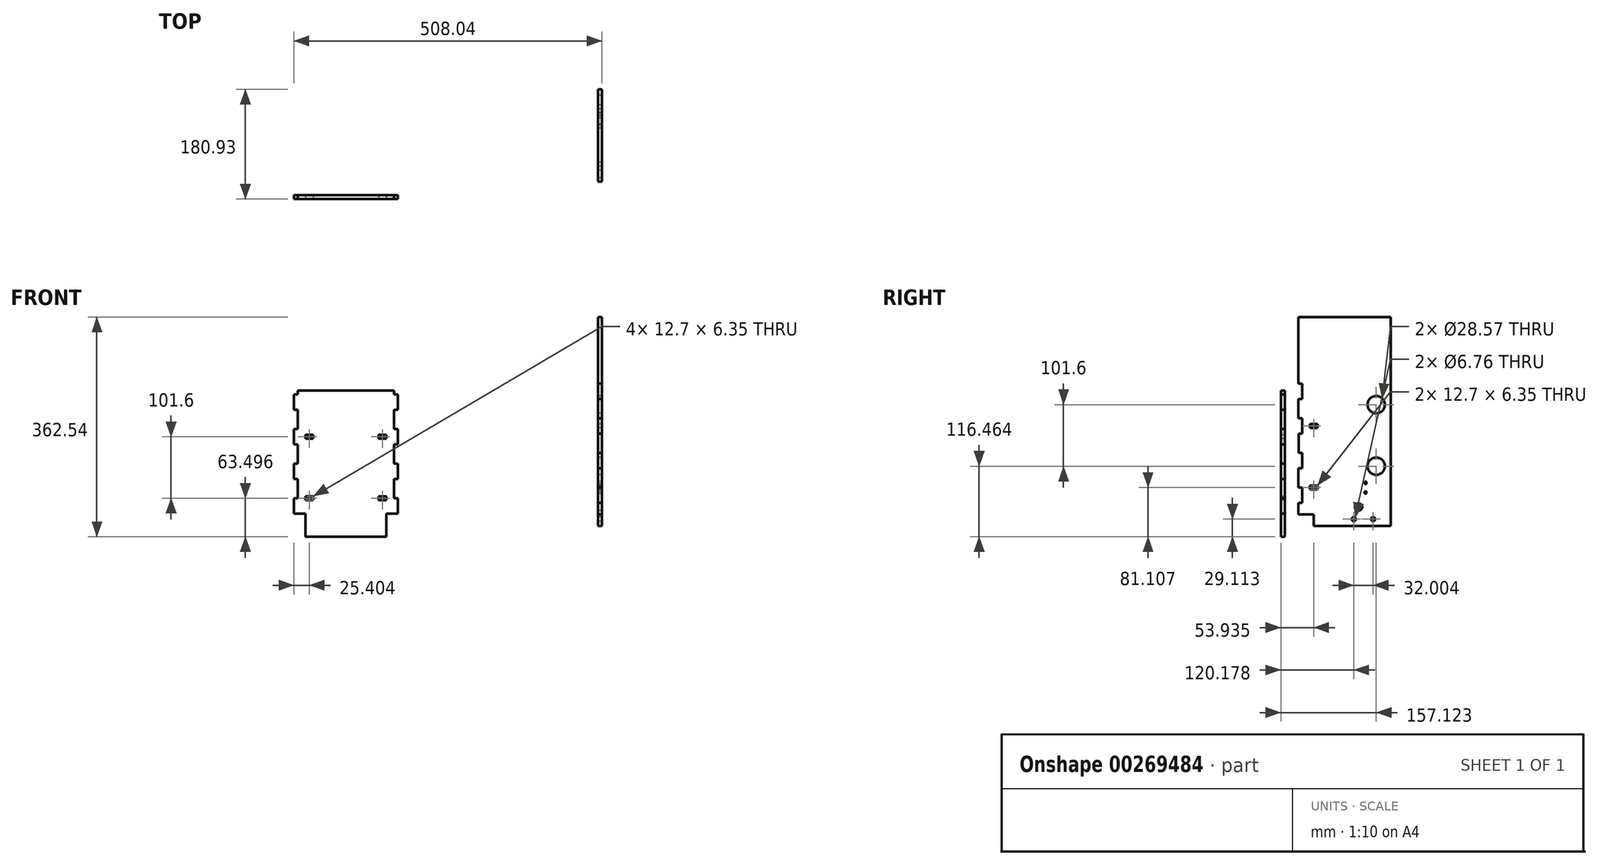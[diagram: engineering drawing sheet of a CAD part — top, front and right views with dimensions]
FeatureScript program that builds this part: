
annotation { "Feature Type Name" : "Feature", "Feature Type Description" : "" }
export const myFeature = defineFeature(function(context is Context, id is Id, definition is map)
    precondition{}
    {
        {
            var Q0;
            Q0=qCreatedBy(makeId("Front.planeOp"),FACE);
            var sketch = newSketch(context, id + "F0", { "sketchPlane" : qUnion([Q0])});
            skLineSegment(sketch, "E0.top", {"start": v(-501.69, -243.4) * mm, "end": v(-330.24, -243.4) * mm});
            skLineSegment(sketch, "E1", {"start": v(-495.34, -2.1) * mm, "end": v(-495.34, -243.4) * mm});
            skLineSegment(sketch, "E2", {"start": v(-501.69, -8.44) * mm, "end": v(-495.34, -8.44) * mm});
            skLineSegment(sketch, "E3", {"start": v(-501.69, -33.84) * mm, "end": v(-495.34, -33.84) * mm});
            skLineSegment(sketch, "E4", {"start": v(-501.69, -65.6) * mm, "end": v(-495.34, -65.6) * mm});
            skLineSegment(sketch, "E5", {"start": v(-501.69, -91) * mm, "end": v(-495.34, -91) * mm});
            skLineSegment(sketch, "E6", {"start": v(-501.69, -122.74) * mm, "end": v(-495.34, -122.74) * mm});
            skLineSegment(sketch, "E7", {"start": v(-501.69, -148.14) * mm, "end": v(-495.34, -148.14) * mm});
            skLineSegment(sketch, "E8", {"start": v(-501.69, -179.9) * mm, "end": v(-495.34, -179.9) * mm});
            skLineSegment(sketch, "E9", {"start": v(-501.69, -205.3) * mm, "end": v(-495.34, -205.3) * mm});
            skLineSegment(sketch, "E10", {"start": v(-501.69, -237.04) * mm, "end": v(-495.34, -237.04) * mm});
            skLineSegment(sketch, "E11", {"start": v(-501.69, -8.44) * mm, "end": v(-501.69, -33.84) * mm});
            skLineSegment(sketch, "E12", {"start": v(-501.69, -65.6) * mm, "end": v(-501.69, -91) * mm});
            skLineSegment(sketch, "E13", {"start": v(-501.69, -122.74) * mm, "end": v(-501.69, -148.14) * mm});
            skLineSegment(sketch, "E14", {"start": v(-501.69, -179.9) * mm, "end": v(-501.69, -205.3) * mm});
            skLineSegment(sketch, "E15", {"start": v(-501.69, -237.04) * mm, "end": v(-501.69, -243.4) * mm});
            skLineSegment(sketch, "E16", {"start": v(-336.59, -2.1) * mm, "end": v(-336.59, -243.4) * mm});
            skLineSegment(sketch, "E17", {"start": v(-336.59, -8.44) * mm, "end": v(-330.24, -8.44) * mm});
            skLineSegment(sketch, "E18", {"start": v(-336.59, -33.84) * mm, "end": v(-330.24, -33.84) * mm});
            skLineSegment(sketch, "E19", {"start": v(-336.59, -65.6) * mm, "end": v(-330.24, -65.6) * mm});
            skLineSegment(sketch, "E20", {"start": v(-336.59, -91) * mm, "end": v(-330.24, -91) * mm});
            skLineSegment(sketch, "E21", {"start": v(-336.59, -122.74) * mm, "end": v(-330.24, -122.74) * mm});
            skLineSegment(sketch, "E22", {"start": v(-336.59, -148.14) * mm, "end": v(-330.24, -148.14) * mm});
            skLineSegment(sketch, "E23", {"start": v(-336.59, -179.9) * mm, "end": v(-330.24, -179.9) * mm});
            skLineSegment(sketch, "E24", {"start": v(-336.59, -205.3) * mm, "end": v(-330.24, -205.3) * mm});
            skLineSegment(sketch, "E25", {"start": v(-336.59, -237.04) * mm, "end": v(-330.24, -237.04) * mm});
            skLineSegment(sketch, "E26", {"start": v(-330.24, -8.44) * mm, "end": v(-330.24, -33.84) * mm});
            skLineSegment(sketch, "E27", {"start": v(-330.24, -65.6) * mm, "end": v(-330.24, -91) * mm});
            skLineSegment(sketch, "E28", {"start": v(-330.24, -122.74) * mm, "end": v(-330.24, -148.14) * mm});
            skLineSegment(sketch, "E29", {"start": v(-330.24, -179.9) * mm, "end": v(-330.24, -205.3) * mm});
            skLineSegment(sketch, "E30", {"start": v(-330.24, -237.04) * mm, "end": v(-330.24, -243.4) * mm});
            skLineSegment(sketch, "E31", {"start": v(-495.34, -2.1) * mm, "end": v(-336.59, -2.1) * mm});
            skSolve(sketch);
        }
        {
            var Q0;
            {var subQ5=sQuery(id+"F0.wireOp",EDGE,"E0.bottom");var subQ8=sQuery(id+"F0.wireOp",EDGE,"E1");var subQ20=makeQuery(id+"F0.imprint","INTERSECT",VERTEX,{"derivedFrom":[subQ5,subQ8]});Q0=makeQuery(id+"F0.imprint","IMPRINT",FACE,{"disambiguationData":[TD([[makeQuery(id+"F0.imprint","IMPRINT",EDGE,{"disambiguationData":[TD([[subQ20,-1.0]])],"derivedFrom":subQ5}),-1.0]])]});}
            var Q1;
            {var subQ4=sQuery(id+"F0.wireOp",EDGE,"LMsAul2w-vVBP-qz1e-n2hl-ZY3DGVZ1hmQM");Q1=makeQuery(id+"F0.imprint","IMPRINT",FACE,{"disambiguationData":[TD([[makeQuery(id+"F0.imprint","IMPRINT",EDGE,{"derivedFrom":subQ4}),1.0]])]});}
            var Q2;
            {var subQ0=sQuery(id+"F0.wireOp",EDGE,"E2");Q2=makeQuery(id+"F0.imprint","IMPRINT",FACE,{"disambiguationData":[TD([[makeQuery(id+"F0.imprint","IMPRINT",EDGE,{"derivedFrom":subQ0}),-1.0]])]});}
            var Q3;
            {var subQ0=sQuery(id+"F0.wireOp",EDGE,"E4");Q3=makeQuery(id+"F0.imprint","IMPRINT",FACE,{"disambiguationData":[TD([[makeQuery(id+"F0.imprint","IMPRINT",EDGE,{"derivedFrom":subQ0}),-1.0]])]});}
            var Q4;
            {var subQ0=sQuery(id+"F0.wireOp",EDGE,"E6");Q4=makeQuery(id+"F0.imprint","IMPRINT",FACE,{"disambiguationData":[TD([[makeQuery(id+"F0.imprint","IMPRINT",EDGE,{"derivedFrom":subQ0}),-1.0]])]});}
            var Q5;
            {var subQ0=sQuery(id+"F0.wireOp",EDGE,"E8");Q5=makeQuery(id+"F0.imprint","IMPRINT",FACE,{"disambiguationData":[TD([[makeQuery(id+"F0.imprint","IMPRINT",EDGE,{"derivedFrom":subQ0}),-1.0]])]});}
            var Q6;
            {var subQ4=sQuery(id+"F0.wireOp",EDGE,"E10");Q6=makeQuery(id+"F0.imprint","IMPRINT",FACE,{"disambiguationData":[TD([[makeQuery(id+"F0.imprint","IMPRINT",EDGE,{"derivedFrom":subQ4}),-1.0]])]});}
            var Q7;
            {var subQ4=sQuery(id+"F0.wireOp",EDGE,"E25");Q7=makeQuery(id+"F0.imprint","IMPRINT",FACE,{"disambiguationData":[TD([[makeQuery(id+"F0.imprint","IMPRINT",EDGE,{"derivedFrom":subQ4}),-1.0]])]});}
            var Q8;
            {var subQ0=sQuery(id+"F0.wireOp",EDGE,"E23");Q8=makeQuery(id+"F0.imprint","IMPRINT",FACE,{"disambiguationData":[TD([[makeQuery(id+"F0.imprint","IMPRINT",EDGE,{"derivedFrom":subQ0}),-1.0]])]});}
            var Q9;
            {var subQ0=sQuery(id+"F0.wireOp",EDGE,"E21");Q9=makeQuery(id+"F0.imprint","IMPRINT",FACE,{"disambiguationData":[TD([[makeQuery(id+"F0.imprint","IMPRINT",EDGE,{"derivedFrom":subQ0}),-1.0]])]});}
            var Q10;
            {var subQ0=sQuery(id+"F0.wireOp",EDGE,"E19");Q10=makeQuery(id+"F0.imprint","IMPRINT",FACE,{"disambiguationData":[TD([[makeQuery(id+"F0.imprint","IMPRINT",EDGE,{"derivedFrom":subQ0}),-1.0]])]});}
            var Q11;
            {var subQ0=sQuery(id+"F0.wireOp",EDGE,"E17");Q11=makeQuery(id+"F0.imprint","IMPRINT",FACE,{"disambiguationData":[TD([[makeQuery(id+"F0.imprint","IMPRINT",EDGE,{"derivedFrom":subQ0}),-1.0]])]});}
            var Q12;
            {var subQ4=sQuery(id+"F0.wireOp",EDGE,"Q2wxjBHx-EqrT-55AE-FTu7-pREpD65ahsZC");Q12=makeQuery(id+"F0.imprint","IMPRINT",FACE,{"disambiguationData":[TD([[makeQuery(id+"F0.imprint","IMPRINT",EDGE,{"derivedFrom":subQ4}),1.0]])]});}
            var Q13;
            {var subQ12=sQuery(id+"F0.wireOp",EDGE,"E31");Q13=makeQuery(id+"F0.imprint","IMPRINT",FACE,{"disambiguationData":[TD([[makeQuery(id+"F0.imprint","IMPRINT",EDGE,{"derivedFrom":subQ12}),-1.0]])]});}
            extrude(context, id + "F1", {"entities" : qUnion([Q0, Q1, Q2, Q3, Q4, Q5, Q6, Q7, Q8, Q9, Q10, Q11, Q12, Q13]), "depth" : 6.35 * mm});
        }
        {
            var Q0;
            Q0=qCreatedBy(makeId("Right.planeOp"),FACE);
            var sketch = newSketch(context, id + "F2", { "sketchPlane" : qUnion([Q0])});
            skLineSegment(sketch, "E32", {"start": v(28.53, -16.23) * mm, "end": v(22.18, -16.23) * mm});
            skLineSegment(sketch, "E33", {"start": v(28.53, -130.53) * mm, "end": v(22.18, -130.53) * mm});
            skLineSegment(sketch, "E34", {"start": v(28.53, -162.28) * mm, "end": v(22.18, -162.28) * mm});
            skLineSegment(sketch, "E35", {"start": v(28.53, -187.68) * mm, "end": v(22.18, -187.68) * mm});
            skLineSegment(sketch, "E36", {"start": v(28.53, -225.78) * mm, "end": v(22.18, -225.78) * mm});
            skLineSegment(sketch, "E37", {"start": v(28.53, -73.38) * mm, "end": v(22.8, -73.38) * mm});
            skLineSegment(sketch, "E38", {"start": v(28.53, -105.13) * mm, "end": v(22.8, -105.13) * mm});
            skLineSegment(sketch, "E39", {"start": v(22.8, -73.38) * mm, "end": v(22.8, -105.13) * mm});
            skLineSegment(sketch, "E40", {"start": v(22.18, -16.23) * mm, "end": v(22.18, -47.98) * mm});
            skLineSegment(sketch, "E41", {"start": v(22.18, -130.53) * mm, "end": v(22.18, -162.28) * mm});
            skLineSegment(sketch, "E42", {"start": v(22.18, -187.68) * mm, "end": v(22.18, -225.78) * mm});
            skLineSegment(sketch, "E43", {"start": v(174.58, -251.18) * mm, "end": v(28.53, -251.18) * mm});
            skLineSegment(sketch, "E44", {"start": v(22.18, 119.15) * mm, "end": v(174.58, 119.15) * mm});
            skLineSegment(sketch, "E45", {"start": v(174.58, 119.15) * mm, "end": v(174.58, -251.18) * mm});
            skLineSegment(sketch, "E46", {"start": v(28.53, -251.18) * mm, "end": v(28.53, 119.15) * mm});
            skLineSegment(sketch, "E47", {"start": v(22.18, -47.98) * mm, "end": v(28.53, -47.98) * mm});
            skLineSegment(sketch, "E48", {"start": v(28.53, 15.52) * mm, "end": v(22.18, 15.52) * mm});
            skLineSegment(sketch, "E49", {"start": v(22.18, 15.52) * mm, "end": v(22.18, 9.17) * mm});
            skLineSegment(sketch, "E50", {"start": v(22.18, 9.17) * mm, "end": v(28.53, 9.17) * mm});
            skLineSegment(sketch, "E51", {"start": v(22.18, 119.15) * mm, "end": v(22.18, 15.52) * mm});
            skLineSegment(sketch, "E52", {"start": v(28.53, -225.78) * mm, "end": v(174.58, -225.78) * mm});
            skLineSegment(sketch, "E53", {"start": v(22.18, -206.73) * mm, "end": v(47.58, -206.73) * mm});
            skLineSegment(sketch, "E54", {"start": v(47.58, -206.73) * mm, "end": v(47.58, -225.78) * mm});
            skSolve(sketch);
        }
        {
            var Q0;
            {var subQ14=sQuery(id+"F2.wireOp",EDGE,"i33fb0zR-01mT-Uh86-wEM1-dtgX8HlX7Fyt");Q0=makeQuery(id+"F2.imprint","IMPRINT",FACE,{"disambiguationData":[TD([[makeQuery(id+"F2.imprint","IMPRINT",EDGE,{"derivedFrom":subQ14}),1.0]])]});}
            var Q1;
            {var subQ4=sQuery(id+"F2.wireOp",EDGE,"rhUE6cCd-mflr-hycs-3UUx-SssaEqSjHUIw");Q1=makeQuery(id+"F2.imprint","IMPRINT",FACE,{"disambiguationData":[TD([[makeQuery(id+"F2.imprint","IMPRINT",EDGE,{"derivedFrom":subQ4}),-1.0]])]});}
            var Q2;
            {var subQ0=sQuery(id+"F2.wireOp",EDGE,"1oS58uJ2-hXIY-gExO-wKBo-R9qEpw5Eswbh");Q2=makeQuery(id+"F2.imprint","IMPRINT",FACE,{"disambiguationData":[TD([[makeQuery(id+"F2.imprint","IMPRINT",EDGE,{"derivedFrom":subQ0}),1.0]])]});}
            var Q3;
            {var subQ0=sQuery(id+"F2.wireOp",EDGE,"HLNgD7Xm-XkV7-PYZ1-Vyr9-8PbT4umlXNnn");Q3=makeQuery(id+"F2.imprint","IMPRINT",FACE,{"disambiguationData":[TD([[makeQuery(id+"F2.imprint","IMPRINT",EDGE,{"derivedFrom":subQ0}),1.0]])]});}
            var Q4;
            {var subQ0=sQuery(id+"F2.wireOp",EDGE,"S2SFkNX2-MHnE-1LtQ-Wrl6-HN21gxM6cwIg.top");Q4=makeQuery(id+"F2.imprint","IMPRINT",FACE,{"disambiguationData":[TD([[makeQuery(id+"F2.imprint","IMPRINT",EDGE,{"derivedFrom":subQ0}),1.0]])]});}
            var Q5;
            {var subQ0=sQuery(id+"F2.wireOp",EDGE,"nHbaO1BD-I0WF-YKfL-4D9o-AtkHzTHVU68h");Q5=makeQuery(id+"F2.imprint","IMPRINT",FACE,{"disambiguationData":[TD([[makeQuery(id+"F2.imprint","IMPRINT",EDGE,{"derivedFrom":subQ0}),1.0]])]});}
            var Q6;
            {var subQ0=sQuery(id+"F2.wireOp",EDGE,"e9KHasA0-oYsS-l2PR-DguL-FNIX4GsAtZwv");Q6=makeQuery(id+"F2.imprint","IMPRINT",FACE,{"disambiguationData":[TD([[makeQuery(id+"F2.imprint","IMPRINT",EDGE,{"derivedFrom":subQ0}),1.0]])]});}
            var Q7;
            {var subQ0=sQuery(id+"F2.wireOp",EDGE,"E37");Q7=makeQuery(id+"F2.imprint","IMPRINT",FACE,{"disambiguationData":[TD([[makeQuery(id+"F2.imprint","IMPRINT",EDGE,{"derivedFrom":subQ0}),1.0]])]});}
            var Q8;
            {var subQ0=sQuery(id+"F2.wireOp",EDGE,"E32");Q8=makeQuery(id+"F2.imprint","IMPRINT",FACE,{"disambiguationData":[TD([[makeQuery(id+"F2.imprint","IMPRINT",EDGE,{"derivedFrom":subQ0}),1.0]])]});}
            var Q9;
            {var subQ0=sQuery(id+"F2.wireOp",EDGE,"gp76ZxvM-iRQH-n3sY-OGDD-mYjBX4D9k2O5");Q9=makeQuery(id+"F2.imprint","IMPRINT",FACE,{"disambiguationData":[TD([[makeQuery(id+"F2.imprint","IMPRINT",EDGE,{"derivedFrom":subQ0}),1.0]])]});}
            var Q10;
            {var subQ0=sQuery(id+"F2.wireOp",EDGE,"E33");Q10=makeQuery(id+"F2.imprint","IMPRINT",FACE,{"disambiguationData":[TD([[makeQuery(id+"F2.imprint","IMPRINT",EDGE,{"derivedFrom":subQ0}),1.0]])]});}
            var Q11;
            {var subQ0=sQuery(id+"F2.wireOp",EDGE,"E35");Q11=makeQuery(id+"F2.imprint","IMPRINT",FACE,{"disambiguationData":[TD([[makeQuery(id+"F2.imprint","IMPRINT",EDGE,{"derivedFrom":subQ0}),1.0]])]});}
            var Q12;
            {var subQ4=sQuery(id+"F2.wireOp",EDGE,"E48");Q12=makeQuery(id+"F2.imprint","IMPRINT",FACE,{"disambiguationData":[TD([[makeQuery(id+"F2.imprint","IMPRINT",EDGE,{"derivedFrom":subQ4}),-1.0]])]});}
            var Q13;
            {var subQ0=sQuery(id+"F2.wireOp",EDGE,"E48");Q13=makeQuery(id+"F2.imprint","IMPRINT",FACE,{"disambiguationData":[TD([[makeQuery(id+"F2.imprint","IMPRINT",EDGE,{"derivedFrom":subQ0}),1.0]])]});}
            var Q14;
            {var subQ6=sQuery(id+"F2.wireOp",EDGE,"E54");Q14=makeQuery(id+"F2.imprint","IMPRINT",FACE,{"disambiguationData":[TD([[makeQuery(id+"F2.imprint","IMPRINT",EDGE,{"derivedFrom":subQ6}),1.0]])]});}
            extrude(context, id + "F3", {"entities" : qUnion([Q0, Q1, Q2, Q3, Q4, Q5, Q6, Q7, Q8, Q9, Q10, Q11, Q12, Q13, Q14]), "depth" : 6.35 * mm});
        }
        {
            var Q0;
            Q0=makeQuery(id+"F3.opExtrude","CAP_FACE",FACE,{"disambiguationData":[OSD([sQuery(id+"F2.wireOp",EDGE,"s0DKLVIk-yI4o-mbJo-Qtl3-NwG1ndSy3CrT"),sQuery(id+"F2.wireOp",EDGE,"E32"),sQuery(id+"F2.wireOp",EDGE,"bUhOaF83-sfzh-5jzX-XBu8-1UuN6AYuXBg6"),sQuery(id+"F2.wireOp",EDGE,"gp76ZxvM-iRQH-n3sY-OGDD-mYjBX4D9k2O5"),sQuery(id+"F2.wireOp",EDGE,"5Qirrqq4-OgZc-HNT0-THzN-mm1dnDsTKt5a"),sQuery(id+"F2.wireOp",EDGE,"E33"),sQuery(id+"F2.wireOp",EDGE,"E34"),sQuery(id+"F2.wireOp",EDGE,"E35"),sQuery(id+"F2.wireOp",EDGE,"E36"),sQuery(id+"F2.wireOp",EDGE,"rhUE6cCd-mflr-hycs-3UUx-SssaEqSjHUIw"),sQuery(id+"F2.wireOp",EDGE,"E37"),sQuery(id+"F2.wireOp",EDGE,"E38"),sQuery(id+"F2.wireOp",EDGE,"XDC90Sgm-SAT4-zVe1-7gUu-QymedyxHn4AY"),sQuery(id+"F2.wireOp",EDGE,"E39"),sQuery(id+"F2.wireOp",EDGE,"E40"),sQuery(id+"F2.wireOp",EDGE,"Gb2Q8Irj-KXKR-EalS-J060-aK0soJo5RwYU"),sQuery(id+"F2.wireOp",EDGE,"E41"),sQuery(id+"F2.wireOp",EDGE,"E42"),sQuery(id+"F2.wireOp",EDGE,"E43"),sQuery(id+"F2.wireOp",EDGE,"E44"),sQuery(id+"F2.wireOp",EDGE,"E45")])],"isStart":true});
            var sketch = newSketch(context, id + "F4", { "sketchPlane" : qUnion([Q0])});
            skCircle(sketch, "E55", {"center": v(-150.77, -126.93) * mm, "radius": 14.29 * mm});
            skCircle(sketch, "E56", {"center": v(-150.77, -25.33) * mm, "radius": 14.29 * mm});
            skSolve(sketch);
        }
        {
            var Q0;
            Q0=makeQuery(id+"F4.imprint","IMPRINT",FACE,{"disambiguationData":[TD([[makeQuery(id+"F4.imprint","IMPRINT",EDGE,{"derivedFrom":sQuery(id+"F4.wireOp",EDGE,"E56")}),1.0]])]});
            var Q1;
            Q1=makeQuery(id+"F4.imprint","IMPRINT",FACE,{"disambiguationData":[TD([[makeQuery(id+"F4.imprint","IMPRINT",EDGE,{"derivedFrom":sQuery(id+"F4.wireOp",EDGE,"E55")}),1.0]])]});
            extrude(context, id + "F5", {"entities" : qUnion([Q0, Q1]), "operationType" : NewBodyOperationType.REMOVE, "oppositeDirection" : true, "depth" : 6.35 * mm});
        }
        {
            var Q0;
            Q0=makeQuery(id+"F3.opExtrude","CAP_FACE",FACE,{"disambiguationData":[OSD([sQuery(id+"F2.wireOp",EDGE,"s0DKLVIk-yI4o-mbJo-Qtl3-NwG1ndSy3CrT"),sQuery(id+"F2.wireOp",EDGE,"E32"),sQuery(id+"F2.wireOp",EDGE,"bUhOaF83-sfzh-5jzX-XBu8-1UuN6AYuXBg6"),sQuery(id+"F2.wireOp",EDGE,"gp76ZxvM-iRQH-n3sY-OGDD-mYjBX4D9k2O5"),sQuery(id+"F2.wireOp",EDGE,"5Qirrqq4-OgZc-HNT0-THzN-mm1dnDsTKt5a"),sQuery(id+"F2.wireOp",EDGE,"E33"),sQuery(id+"F2.wireOp",EDGE,"E34"),sQuery(id+"F2.wireOp",EDGE,"E35"),sQuery(id+"F2.wireOp",EDGE,"E36"),sQuery(id+"F2.wireOp",EDGE,"rhUE6cCd-mflr-hycs-3UUx-SssaEqSjHUIw"),sQuery(id+"F2.wireOp",EDGE,"E37"),sQuery(id+"F2.wireOp",EDGE,"E38"),sQuery(id+"F2.wireOp",EDGE,"XDC90Sgm-SAT4-zVe1-7gUu-QymedyxHn4AY"),sQuery(id+"F2.wireOp",EDGE,"E39"),sQuery(id+"F2.wireOp",EDGE,"E40"),sQuery(id+"F2.wireOp",EDGE,"Gb2Q8Irj-KXKR-EalS-J060-aK0soJo5RwYU"),sQuery(id+"F2.wireOp",EDGE,"E41"),sQuery(id+"F2.wireOp",EDGE,"E42"),sQuery(id+"F2.wireOp",EDGE,"E43"),sQuery(id+"F2.wireOp",EDGE,"E44"),sQuery(id+"F2.wireOp",EDGE,"E45")])],"isStart":true});
            var sketch = newSketch(context, id + "F6", { "sketchPlane" : qUnion([Q0])});
            skLineSegment(sketch, "E57.bottom", {"start": v(-53.93, -159.1) * mm, "end": v(-41.23, -159.1) * mm});
            skLineSegment(sketch, "E57.top", {"start": v(-53.93, -165.46) * mm, "end": v(-41.23, -165.46) * mm});
            skLineSegment(sketch, "E57.left", {"start": v(-53.93, -159.1) * mm, "end": v(-53.93, -165.46) * mm});
            skLineSegment(sketch, "E57.right", {"start": v(-41.23, -159.1) * mm, "end": v(-41.23, -165.46) * mm});
            skLineSegment(sketch, "E58.bottom", {"start": v(-53.93, -57.5) * mm, "end": v(-41.23, -57.5) * mm});
            skLineSegment(sketch, "E58.top", {"start": v(-53.93, -63.86) * mm, "end": v(-41.23, -63.86) * mm});
            skLineSegment(sketch, "E58.left", {"start": v(-53.93, -57.5) * mm, "end": v(-53.93, -63.86) * mm});
            skLineSegment(sketch, "E58.right", {"start": v(-41.23, -57.5) * mm, "end": v(-41.23, -63.86) * mm});
            skSolve(sketch);
        }
        {
            var Q0;
            Q0=makeQuery(id+"F6.imprint","IMPRINT",FACE,{"disambiguationData":[TD([[makeQuery(id+"F6.imprint","IMPRINT",EDGE,{"derivedFrom":sQuery(id+"F6.wireOp",EDGE,"zmTBmbvl-Oux8-fxHu-hAO5-6Uis3kAJMw4c.bottom")}),-1.0]])]});
            var Q1;
            Q1=makeQuery(id+"F6.imprint","IMPRINT",FACE,{"disambiguationData":[TD([[makeQuery(id+"F6.imprint","IMPRINT",EDGE,{"derivedFrom":sQuery(id+"F6.wireOp",EDGE,"E58.bottom")}),-1.0]])]});
            var Q2;
            Q2=makeQuery(id+"F6.imprint","IMPRINT",FACE,{"disambiguationData":[TD([[makeQuery(id+"F6.imprint","IMPRINT",EDGE,{"derivedFrom":sQuery(id+"F6.wireOp",EDGE,"E57.bottom")}),-1.0]])]});
            extrude(context, id + "F7", {"entities" : qUnion([Q0, Q1, Q2]), "operationType" : NewBodyOperationType.REMOVE, "oppositeDirection" : true, "depth" : 6.35 * mm});
        }
        {
            var Q0;
            Q0=makeQuery(id+"F1.opExtrude","CAP_FACE",FACE,{"disambiguationData":[OSD([sQuery(id+"F0.wireOp",EDGE,"E0.bottom"),sQuery(id+"F0.wireOp",EDGE,"E0.top"),sQuery(id+"F0.wireOp",EDGE,"E1"),sQuery(id+"F0.wireOp",EDGE,"LMsAul2w-vVBP-qz1e-n2hl-ZY3DGVZ1hmQM"),sQuery(id+"F0.wireOp",EDGE,"E2"),sQuery(id+"F0.wireOp",EDGE,"E3"),sQuery(id+"F0.wireOp",EDGE,"E4"),sQuery(id+"F0.wireOp",EDGE,"E5"),sQuery(id+"F0.wireOp",EDGE,"E6"),sQuery(id+"F0.wireOp",EDGE,"E7"),sQuery(id+"F0.wireOp",EDGE,"E8"),sQuery(id+"F0.wireOp",EDGE,"E9"),sQuery(id+"F0.wireOp",EDGE,"E10"),sQuery(id+"F0.wireOp",EDGE,"fckjmxOd-PKS0-K6HS-jWLe-0Rm2YWeLxNei"),sQuery(id+"F0.wireOp",EDGE,"E11"),sQuery(id+"F0.wireOp",EDGE,"E12"),sQuery(id+"F0.wireOp",EDGE,"E13"),sQuery(id+"F0.wireOp",EDGE,"E14"),sQuery(id+"F0.wireOp",EDGE,"E15"),sQuery(id+"F0.wireOp",EDGE,"E16"),sQuery(id+"F0.wireOp",EDGE,"Q2wxjBHx-EqrT-55AE-FTu7-pREpD65ahsZC"),sQuery(id+"F0.wireOp",EDGE,"E17"),sQuery(id+"F0.wireOp",EDGE,"E18"),sQuery(id+"F0.wireOp",EDGE,"E19"),sQuery(id+"F0.wireOp",EDGE,"E20"),sQuery(id+"F0.wireOp",EDGE,"E21"),sQuery(id+"F0.wireOp",EDGE,"E22"),sQuery(id+"F0.wireOp",EDGE,"E23"),sQuery(id+"F0.wireOp",EDGE,"E24"),sQuery(id+"F0.wireOp",EDGE,"E25"),sQuery(id+"F0.wireOp",EDGE,"p0LhYthy-u7VA-cxhh-v3hJ-NGUNxxqC1vMh"),sQuery(id+"F0.wireOp",EDGE,"E26"),sQuery(id+"F0.wireOp",EDGE,"E27"),sQuery(id+"F0.wireOp",EDGE,"E28"),sQuery(id+"F0.wireOp",EDGE,"E29"),sQuery(id+"F0.wireOp",EDGE,"E30")])],"isStart":false});
            var sketch = newSketch(context, id + "F8", { "sketchPlane" : qUnion([Q0])});
            skLineSegment(sketch, "E59.bottom", {"start": v(-482.64, -75.12) * mm, "end": v(-469.94, -75.12) * mm});
            skLineSegment(sketch, "E59.top", {"start": v(-482.64, -81.47) * mm, "end": v(-469.94, -81.47) * mm});
            skLineSegment(sketch, "E59.left", {"start": v(-482.64, -75.12) * mm, "end": v(-482.64, -81.47) * mm});
            skLineSegment(sketch, "E59.right", {"start": v(-469.94, -75.12) * mm, "end": v(-469.94, -81.47) * mm});
            skLineSegment(sketch, "E60.bottom", {"start": v(-482.64, -176.72) * mm, "end": v(-469.94, -176.72) * mm});
            skLineSegment(sketch, "E60.top", {"start": v(-482.64, -183.07) * mm, "end": v(-469.94, -183.07) * mm});
            skLineSegment(sketch, "E60.left", {"start": v(-482.64, -176.72) * mm, "end": v(-482.64, -183.07) * mm});
            skLineSegment(sketch, "E60.right", {"start": v(-469.94, -176.72) * mm, "end": v(-469.94, -183.07) * mm});
            skLineSegment(sketch, "E61.bottom", {"start": v(-361.99, -75.12) * mm, "end": v(-349.29, -75.12) * mm});
            skLineSegment(sketch, "E61.top", {"start": v(-361.99, -81.47) * mm, "end": v(-349.29, -81.47) * mm});
            skLineSegment(sketch, "E61.left", {"start": v(-361.99, -75.12) * mm, "end": v(-361.99, -81.47) * mm});
            skLineSegment(sketch, "E61.right", {"start": v(-349.29, -75.12) * mm, "end": v(-349.29, -81.47) * mm});
            skLineSegment(sketch, "E62.bottom", {"start": v(-361.99, -176.72) * mm, "end": v(-349.29, -176.72) * mm});
            skLineSegment(sketch, "E62.top", {"start": v(-361.99, -183.07) * mm, "end": v(-349.29, -183.07) * mm});
            skLineSegment(sketch, "E62.left", {"start": v(-361.99, -176.72) * mm, "end": v(-361.99, -183.07) * mm});
            skLineSegment(sketch, "E62.right", {"start": v(-349.29, -176.72) * mm, "end": v(-349.29, -183.07) * mm});
            skSolve(sketch);
        }
        {
            var Q0;
            Q0 = qSketchRegion(id + "F8", true);
            extrude(context, id + "F9", {"entities" : qUnion([Q0]), "operationType" : NewBodyOperationType.REMOVE, "oppositeDirection" : true, "depth" : 6.35 * mm});
        }
        {
            var Q0;
            Q0=makeQuery(id+"F1.opExtrude","CAP_FACE",FACE,{"disambiguationData":[OSD([sQuery(id+"F0.wireOp",EDGE,"E0.top"),sQuery(id+"F0.wireOp",EDGE,"E1"),sQuery(id+"F0.wireOp",EDGE,"E2"),sQuery(id+"F0.wireOp",EDGE,"E3"),sQuery(id+"F0.wireOp",EDGE,"E4"),sQuery(id+"F0.wireOp",EDGE,"E5"),sQuery(id+"F0.wireOp",EDGE,"E6"),sQuery(id+"F0.wireOp",EDGE,"E7"),sQuery(id+"F0.wireOp",EDGE,"E8"),sQuery(id+"F0.wireOp",EDGE,"E9"),sQuery(id+"F0.wireOp",EDGE,"E10"),sQuery(id+"F0.wireOp",EDGE,"E11"),sQuery(id+"F0.wireOp",EDGE,"E12"),sQuery(id+"F0.wireOp",EDGE,"E13"),sQuery(id+"F0.wireOp",EDGE,"E14"),sQuery(id+"F0.wireOp",EDGE,"E15"),sQuery(id+"F0.wireOp",EDGE,"E16"),sQuery(id+"F0.wireOp",EDGE,"E17"),sQuery(id+"F0.wireOp",EDGE,"E18"),sQuery(id+"F0.wireOp",EDGE,"E19"),sQuery(id+"F0.wireOp",EDGE,"E20"),sQuery(id+"F0.wireOp",EDGE,"E21"),sQuery(id+"F0.wireOp",EDGE,"E22"),sQuery(id+"F0.wireOp",EDGE,"E23"),sQuery(id+"F0.wireOp",EDGE,"E24"),sQuery(id+"F0.wireOp",EDGE,"E25"),sQuery(id+"F0.wireOp",EDGE,"E26"),sQuery(id+"F0.wireOp",EDGE,"E27"),sQuery(id+"F0.wireOp",EDGE,"E28"),sQuery(id+"F0.wireOp",EDGE,"E29"),sQuery(id+"F0.wireOp",EDGE,"E30"),sQuery(id+"F0.wireOp",EDGE,"E31")])],"isStart":false});
            var sketch = newSketch(context, id + "F10", { "sketchPlane" : qUnion([Q0])});
            skLineSegment(sketch, "E63", {"start": v(-482.64, -243.4) * mm, "end": v(-482.64, -205.3) * mm});
            skLineSegment(sketch, "E64", {"start": v(-482.64, -205.3) * mm, "end": v(-501.69, -205.3) * mm});
            skLineSegment(sketch, "E65", {"start": v(-501.69, -205.3) * mm, "end": v(-501.69, -243.4) * mm});
            skLineSegment(sketch, "E66.bottom", {"start": v(-330.24, -243.4) * mm, "end": v(-349.29, -243.4) * mm});
            skLineSegment(sketch, "E66.top", {"start": v(-330.24, -205.3) * mm, "end": v(-349.29, -205.3) * mm});
            skLineSegment(sketch, "E66.left", {"start": v(-330.24, -243.4) * mm, "end": v(-330.24, -205.3) * mm});
            skLineSegment(sketch, "E66.right", {"start": v(-349.29, -243.4) * mm, "end": v(-349.29, -205.3) * mm});
            skSolve(sketch);
        }
        {
            var Q0;
            {var subQ3=sQuery(id+"F10.wireOp",EDGE,"E63");Q0=makeQuery(id+"F10.imprint","IMPRINT",FACE,{"disambiguationData":[TD([[makeQuery(id+"F10.imprint","IMPRINT",EDGE,{"derivedFrom":subQ3}),1.0]])]});}
            var Q1;
            {var subQ2=sQuery(id+"F10.wireOp",EDGE,"E66.bottom");Q1=makeQuery(id+"F10.imprint","IMPRINT",FACE,{"disambiguationData":[TD([[makeQuery(id+"F10.imprint","IMPRINT",EDGE,{"derivedFrom":subQ2}),1.0]])]});}
            extrude(context, id + "F11", {"entities" : qUnion([Q0, Q1]), "operationType" : NewBodyOperationType.REMOVE, "oppositeDirection" : true, "depth" : 6.35 * mm});
        }
        {
            var Q0;
            Q0=makeQuery(id+"F3.opExtrude","CAP_FACE",FACE,{"disambiguationData":[OSD([sQuery(id+"F2.wireOp",EDGE,"E32"),sQuery(id+"F2.wireOp",EDGE,"E33"),sQuery(id+"F2.wireOp",EDGE,"E34"),sQuery(id+"F2.wireOp",EDGE,"E35"),sQuery(id+"F2.wireOp",EDGE,"E37"),sQuery(id+"F2.wireOp",EDGE,"E38"),sQuery(id+"F2.wireOp",EDGE,"E39"),sQuery(id+"F2.wireOp",EDGE,"E40"),sQuery(id+"F2.wireOp",EDGE,"E41"),sQuery(id+"F2.wireOp",EDGE,"E42"),sQuery(id+"F2.wireOp",EDGE,"E44"),sQuery(id+"F2.wireOp",EDGE,"E45"),sQuery(id+"F2.wireOp",EDGE,"E46"),sQuery(id+"F2.wireOp",EDGE,"E47"),sQuery(id+"F2.wireOp",EDGE,"E49"),sQuery(id+"F2.wireOp",EDGE,"E50"),sQuery(id+"F2.wireOp",EDGE,"E51"),sQuery(id+"F2.wireOp",EDGE,"E52"),sQuery(id+"F2.wireOp",EDGE,"E53"),sQuery(id+"F2.wireOp",EDGE,"E54")])],"isStart":true});
            var sketch = newSketch(context, id + "F12", { "sketchPlane" : qUnion([Q0])});
            skCircle(sketch, "E67", {"center": v(-121.63, -194.31) * mm, "radius": 6 * mm});
            skSolve(sketch);
        }
        {
            var Q0;
            Q0=makeQuery(id+"F12.imprint","IMPRINT",FACE,{"disambiguationData":[TD([[makeQuery(id+"F12.imprint","IMPRINT",EDGE,{"derivedFrom":sQuery(id+"F12.wireOp",EDGE,"E67")}),1.0]])]});
            var Q1;
            Q1=sQuery(id+"F12.wireOp",EDGE,"E67");
            extrude(context, id + "F13", {"entities" : qUnion([Q0]), "operationType" : NewBodyOperationType.REMOVE, "surfaceEntities" : qUnion([Q1]), "oppositeDirection" : true, "depth" : 25.4 * mm});
        }
        {
            var Q0;
            Q0=makeQuery(id+"F3.opExtrude","CAP_FACE",FACE,{"disambiguationData":[OSD([sQuery(id+"F2.wireOp",EDGE,"E32"),sQuery(id+"F2.wireOp",EDGE,"E33"),sQuery(id+"F2.wireOp",EDGE,"E34"),sQuery(id+"F2.wireOp",EDGE,"E35"),sQuery(id+"F2.wireOp",EDGE,"E37"),sQuery(id+"F2.wireOp",EDGE,"E38"),sQuery(id+"F2.wireOp",EDGE,"E39"),sQuery(id+"F2.wireOp",EDGE,"E40"),sQuery(id+"F2.wireOp",EDGE,"E41"),sQuery(id+"F2.wireOp",EDGE,"E42"),sQuery(id+"F2.wireOp",EDGE,"E44"),sQuery(id+"F2.wireOp",EDGE,"E45"),sQuery(id+"F2.wireOp",EDGE,"E46"),sQuery(id+"F2.wireOp",EDGE,"E47"),sQuery(id+"F2.wireOp",EDGE,"E49"),sQuery(id+"F2.wireOp",EDGE,"E50"),sQuery(id+"F2.wireOp",EDGE,"E51"),sQuery(id+"F2.wireOp",EDGE,"E52"),sQuery(id+"F2.wireOp",EDGE,"E53"),sQuery(id+"F2.wireOp",EDGE,"E54")])],"isStart":true});
            var sketch = newSketch(context, id + "F14", { "sketchPlane" : qUnion([Q0])});
            skCircle(sketch, "E68", {"center": v(-145.83, -214.28) * mm, "radius": 3.38 * mm});
            skCircle(sketch, "E69", {"center": v(-113.83, -214.28) * mm, "radius": 3.38 * mm});
            skCircle(sketch, "E70", {"center": v(-133.2, -154.38) * mm, "radius": 1.9 * mm});
            skCircle(sketch, "E71", {"center": v(-133.2, -170.39) * mm, "radius": 1.9 * mm});
            skSolve(sketch);
        }
        {
            var Q0;
            Q0=makeQuery(id+"F14.imprint","IMPRINT",FACE,{"disambiguationData":[TD([[makeQuery(id+"F14.imprint","IMPRINT",EDGE,{"derivedFrom":sQuery(id+"F14.wireOp",EDGE,"E68")}),1.0]])]});
            var Q1;
            Q1=makeQuery(id+"F14.imprint","IMPRINT",FACE,{"disambiguationData":[TD([[makeQuery(id+"F14.imprint","IMPRINT",EDGE,{"derivedFrom":sQuery(id+"F14.wireOp",EDGE,"E69")}),1.0]])]});
            var Q2;
            Q2=makeQuery(id+"F14.imprint","IMPRINT",FACE,{"disambiguationData":[TD([[makeQuery(id+"F14.imprint","IMPRINT",EDGE,{"derivedFrom":sQuery(id+"F14.wireOp",EDGE,"E71")}),1.0]])]});
            var Q3;
            Q3=makeQuery(id+"F14.imprint","IMPRINT",FACE,{"disambiguationData":[TD([[makeQuery(id+"F14.imprint","IMPRINT",EDGE,{"derivedFrom":sQuery(id+"F14.wireOp",EDGE,"E70")}),1.0]])]});
            extrude(context, id + "F15", {"entities" : qUnion([Q0, Q1, Q2, Q3]), "operationType" : NewBodyOperationType.REMOVE, "oppositeDirection" : true, "depth" : 6.35 * mm});
        }
    });
